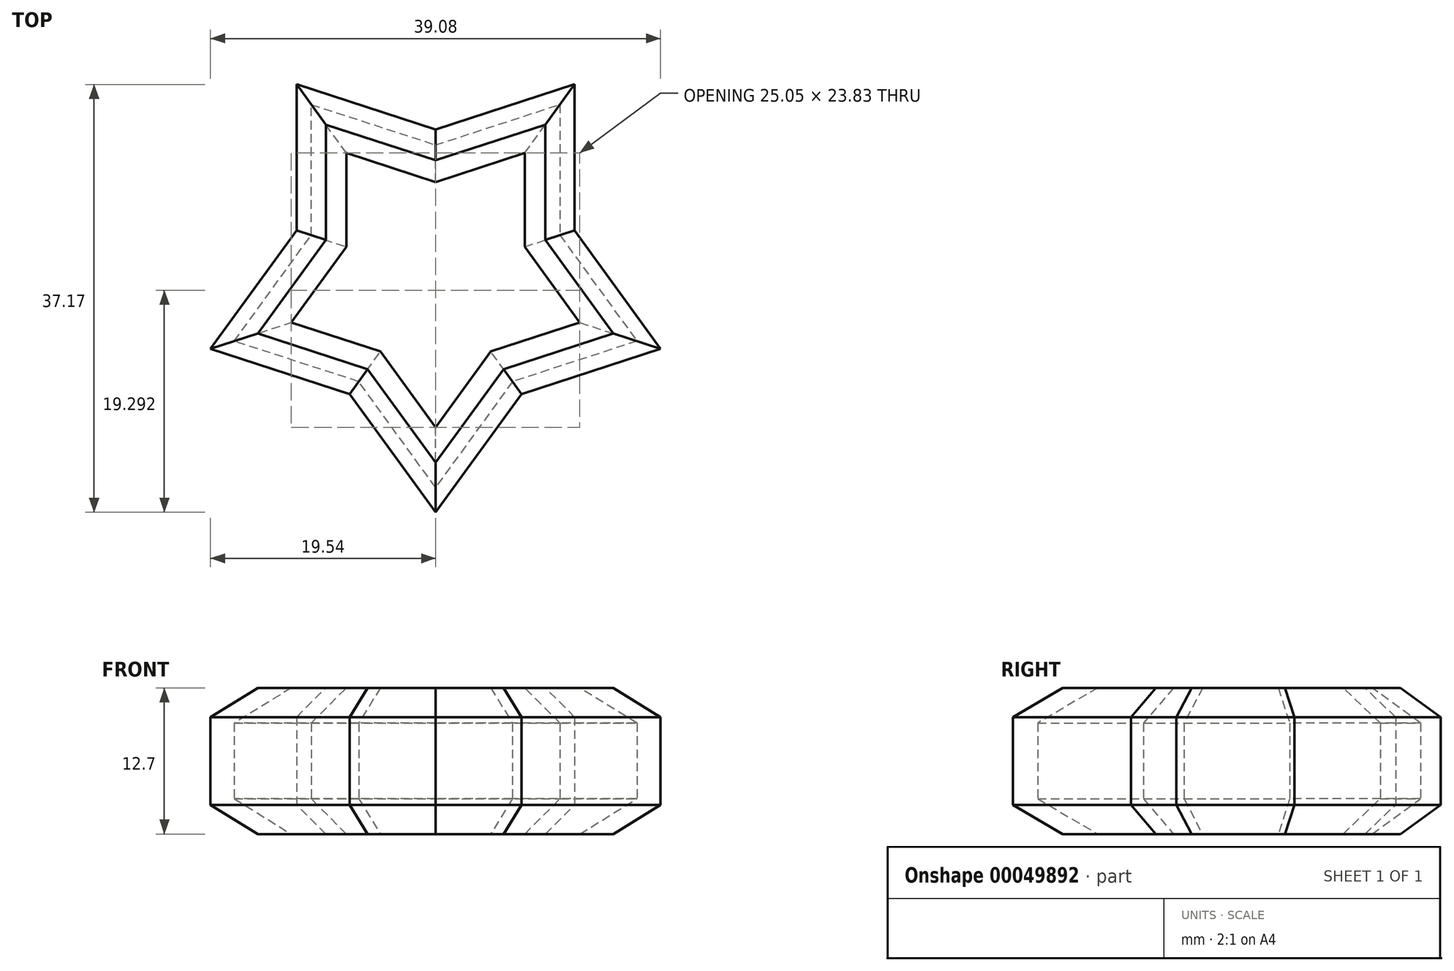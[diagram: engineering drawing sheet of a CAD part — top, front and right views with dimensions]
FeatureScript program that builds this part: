
annotation { "Feature Type Name" : "Feature", "Feature Type Description" : "" }
export const myFeature = defineFeature(function(context is Context, id is Id, definition is map)
    precondition{}
    {
        {
            var Q0;
            Q0=qCreatedBy(makeId("Top.planeOp"),FACE);
            var sketch = newSketch(context, id + "F0", { "sketchPlane" : qUnion([Q0])});
            skCircle(sketch, "E0.cCircle", {"center": v(0, 0) * mm, "radius": 16.62 * mm, "construction": true});
            skLineSegment(sketch, "E0.0", {"start": v(0, -20.55) * mm, "end": v(-19.54, -6.35) * mm});
            skLineSegment(sketch, "E0.1", {"start": v(-19.54, -6.35) * mm, "end": v(-12.08, 16.62) * mm});
            skLineSegment(sketch, "E0.2", {"start": v(-12.08, 16.62) * mm, "end": v(12.08, 16.62) * mm});
            skLineSegment(sketch, "E0.3", {"start": v(12.08, 16.62) * mm, "end": v(19.54, -6.35) * mm});
            skLineSegment(sketch, "E0.4", {"start": v(19.54, -6.35) * mm, "end": v(0, -20.55) * mm});
            skPoint(sketch, "E0.0.midPoint", {"position": v(-9.77, -13.45) * mm});
            skLineSegment(sketch, "E1", {"start": v(12.08, 16.62) * mm, "end": v(0, 12.7) * mm});
            skLineSegment(sketch, "E2", {"start": v(0, 12.7) * mm, "end": v(-12.08, 16.62) * mm});
            skLineSegment(sketch, "E3", {"start": v(-12.08, 16.62) * mm, "end": v(-12.08, 3.92) * mm});
            skLineSegment(sketch, "E4", {"start": v(-12.08, 3.92) * mm, "end": v(-19.54, -6.35) * mm});
            skLineSegment(sketch, "E5", {"start": v(-19.54, -6.35) * mm, "end": v(-7.46, -10.27) * mm});
            skLineSegment(sketch, "E6", {"start": v(-7.46, -10.27) * mm, "end": v(0, -20.55) * mm});
            skLineSegment(sketch, "E7", {"start": v(0, -20.55) * mm, "end": v(7.46, -10.27) * mm});
            skLineSegment(sketch, "E8", {"start": v(7.46, -10.27) * mm, "end": v(19.54, -6.35) * mm});
            skLineSegment(sketch, "E9", {"start": v(19.54, -6.35) * mm, "end": v(12.08, 3.92) * mm});
            skLineSegment(sketch, "E10", {"start": v(12.08, 3.92) * mm, "end": v(12.08, 16.62) * mm});
            skSolve(sketch);
        }
        {
            var Q0;
            Q0=makeQuery(id+"F0.imprint","IMPRINT",FACE,{"disambiguationData":[TD([[makeQuery(id+"F0.imprint","IMPRINT",EDGE,{"derivedFrom":sQuery(id+"F0.wireOp",EDGE,"E1")}),1.0]])]});
            extrude(context, id + "F1", {"entities" : qUnion([Q0]), "depth" : 12.7 * mm});
        }
        {
            var Q0;
            Q0=makeQuery(id+"F1.opExtrude","CAP_EDGE",EDGE,{"disambiguationData":[OSD([sQuery(id+"F0.wireOp",EDGE,"E6")])],"isStart":false});
            var Q1;
            Q1=makeQuery(id+"F1.opExtrude","CAP_EDGE",EDGE,{"disambiguationData":[OSD([sQuery(id+"F0.wireOp",EDGE,"E7")])],"isStart":false});
            var Q2;
            Q2=makeQuery(id+"F1.opExtrude","CAP_EDGE",EDGE,{"disambiguationData":[OSD([sQuery(id+"F0.wireOp",EDGE,"E8")])],"isStart":false});
            var Q3;
            Q3=makeQuery(id+"F1.opExtrude","CAP_EDGE",EDGE,{"disambiguationData":[OSD([sQuery(id+"F0.wireOp",EDGE,"E9")])],"isStart":false});
            var Q4;
            Q4=makeQuery(id+"F1.opExtrude","CAP_EDGE",EDGE,{"disambiguationData":[OSD([sQuery(id+"F0.wireOp",EDGE,"E10")])],"isStart":false});
            var Q5;
            Q5=makeQuery(id+"F1.opExtrude","CAP_EDGE",EDGE,{"disambiguationData":[OSD([sQuery(id+"F0.wireOp",EDGE,"E1")])],"isStart":false});
            var Q6;
            Q6=makeQuery(id+"F1.opExtrude","CAP_EDGE",EDGE,{"disambiguationData":[OSD([sQuery(id+"F0.wireOp",EDGE,"E2")])],"isStart":false});
            var Q7;
            Q7=makeQuery(id+"F1.opExtrude","CAP_EDGE",EDGE,{"disambiguationData":[OSD([sQuery(id+"F0.wireOp",EDGE,"E3")])],"isStart":false});
            var Q8;
            Q8=makeQuery(id+"F1.opExtrude","CAP_EDGE",EDGE,{"disambiguationData":[OSD([sQuery(id+"F0.wireOp",EDGE,"E4")])],"isStart":false});
            var Q9;
            Q9=makeQuery(id+"F1.opExtrude","CAP_EDGE",EDGE,{"disambiguationData":[OSD([sQuery(id+"F0.wireOp",EDGE,"E5")])],"isStart":false});
            var Q10;
            Q10=makeQuery(id+"F1.opExtrude","CAP_FACE",FACE,{"disambiguationData":[OSD([sQuery(id+"F0.wireOp",EDGE,"E1"),sQuery(id+"F0.wireOp",EDGE,"E2"),sQuery(id+"F0.wireOp",EDGE,"E3"),sQuery(id+"F0.wireOp",EDGE,"E4"),sQuery(id+"F0.wireOp",EDGE,"E5"),sQuery(id+"F0.wireOp",EDGE,"E6"),sQuery(id+"F0.wireOp",EDGE,"E7"),sQuery(id+"F0.wireOp",EDGE,"E8"),sQuery(id+"F0.wireOp",EDGE,"E9"),sQuery(id+"F0.wireOp",EDGE,"E10")])],"isStart":true});
            chamfer(context, id + "F2", {"entities" : qUnion([Q0, Q1, Q2, Q3, Q4, Q5, Q6, Q7, Q8, Q9, Q10]), "width" : 2.54 * mm, "tangentPropagation" : true});
        }
        {
            var Q0;
            Q0=makeQuery(id+"F1.opExtrude","CAP_FACE",FACE,{"disambiguationData":[OSD([sQuery(id+"F0.wireOp",EDGE,"E1"),sQuery(id+"F0.wireOp",EDGE,"E2"),sQuery(id+"F0.wireOp",EDGE,"E3"),sQuery(id+"F0.wireOp",EDGE,"E4"),sQuery(id+"F0.wireOp",EDGE,"E5"),sQuery(id+"F0.wireOp",EDGE,"E6"),sQuery(id+"F0.wireOp",EDGE,"E7"),sQuery(id+"F0.wireOp",EDGE,"E8"),sQuery(id+"F0.wireOp",EDGE,"E9"),sQuery(id+"F0.wireOp",EDGE,"E10")])],"isStart":true});
            var Q1;
            Q1=makeQuery(id+"F1.opExtrude","CAP_FACE",FACE,{"disambiguationData":[OSD([sQuery(id+"F0.wireOp",EDGE,"E1"),sQuery(id+"F0.wireOp",EDGE,"E2"),sQuery(id+"F0.wireOp",EDGE,"E3"),sQuery(id+"F0.wireOp",EDGE,"E4"),sQuery(id+"F0.wireOp",EDGE,"E5"),sQuery(id+"F0.wireOp",EDGE,"E6"),sQuery(id+"F0.wireOp",EDGE,"E7"),sQuery(id+"F0.wireOp",EDGE,"E8"),sQuery(id+"F0.wireOp",EDGE,"E9"),sQuery(id+"F0.wireOp",EDGE,"E10")])],"isStart":false});
            shell(context, id + "F3", {"entities" : qUnion([Q0, Q1]), "thickness" : 1.27 * mm});
        }
    });
